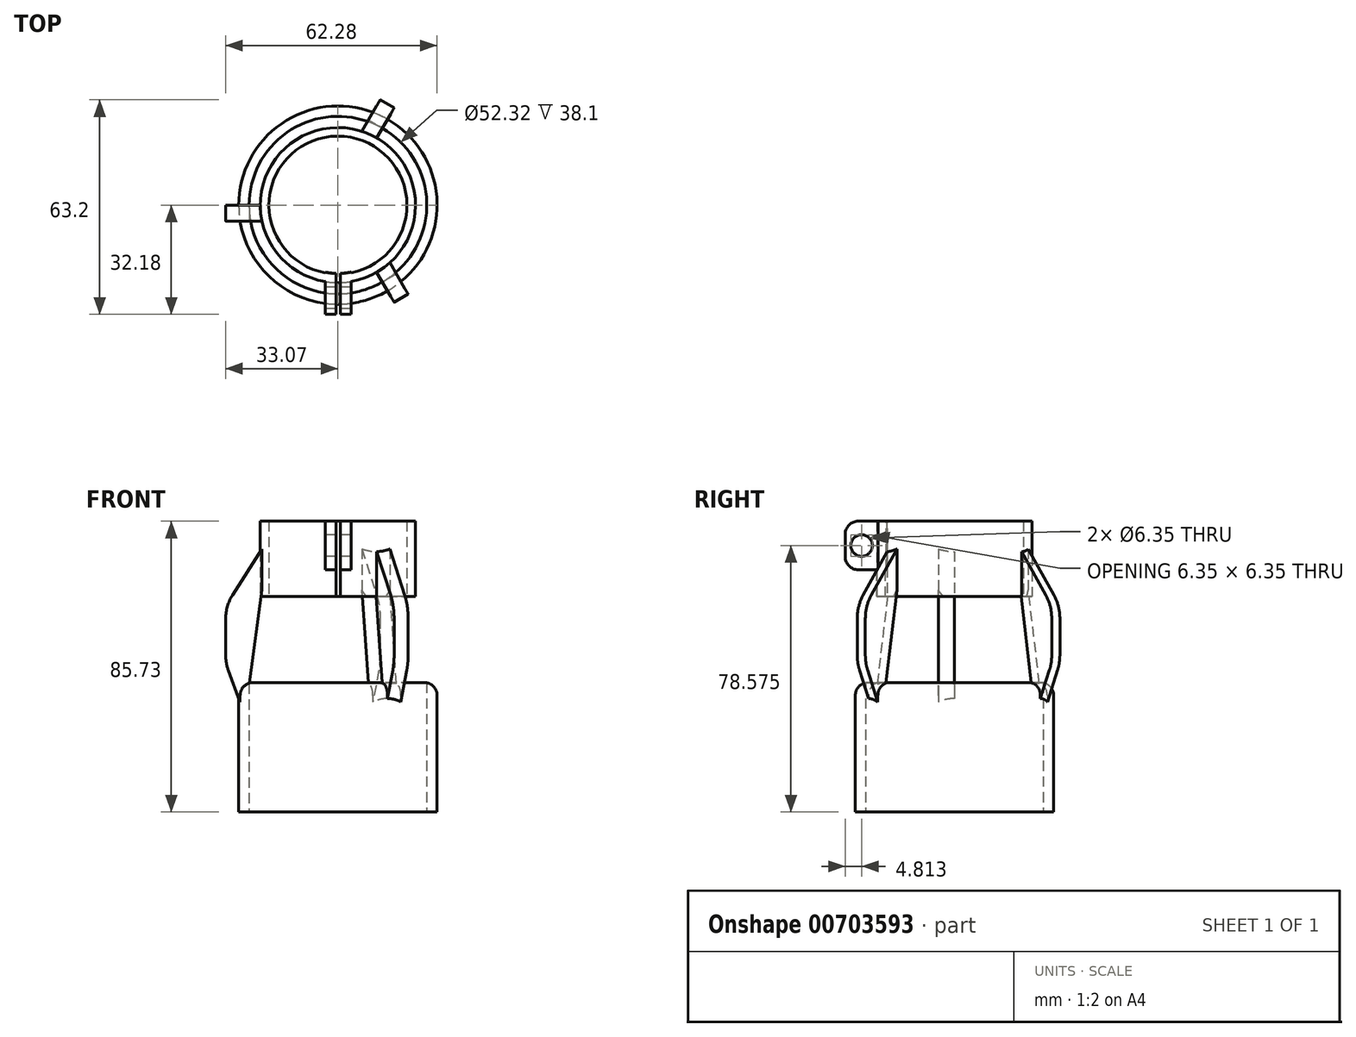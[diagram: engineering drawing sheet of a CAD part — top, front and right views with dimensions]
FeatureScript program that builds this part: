
annotation { "Feature Type Name" : "Feature", "Feature Type Description" : "" }
export const myFeature = defineFeature(function(context is Context, id is Id, definition is map)
    precondition{}
    {
        {
            var Q0;
            Q0=qCreatedBy(makeId("Top.planeOp"),FACE);
            var sketch = newSketch(context, id + "F0", { "sketchPlane" : qUnion([Q0])});
            skCircle(sketch, "E0", {"center": v(0, 0) * mm, "radius": 29.2 * mm});
            skCircle(sketch, "E1", {"center": v(0, 0) * mm, "radius": 26.16 * mm});
            skSolve(sketch);
        }
        {
            var Q0;
            Q0 = qSketchRegion(id + "F0", true);
            extrude(context, id + "F1", {"entities" : qUnion([Q0]), "depth" : 38.1 * mm, "offsetDistance" : 25.4 * mm});
        }
        {
            var Q0;
            Q0=makeQuery(id+"F1.opExtrude","CAP_FACE",FACE,{"disambiguationData":[OSD([sQuery(id+"F0.wireOp",EDGE,"E0"),sQuery(id+"F0.wireOp",EDGE,"E1")])],"isStart":false});
            cPlane(context, id + "F2", {"entities" : qUnion([Q0]), "cplaneType" : CPlaneType.OFFSET, "offset" : 25.4 * mm, "width" : 152.4 * mm, "height" : 152.4 * mm});
        }
        {
            var Q0;
            Q0=qCreatedBy(id+"F2.planeOp",FACE);
            var sketch = newSketch(context, id + "F3", { "sketchPlane" : qUnion([Q0])});
            skCircle(sketch, "E2", {"center": v(0, 0) * mm, "radius": 20.32 * mm});
            skCircle(sketch, "E3", {"center": v(0, 0) * mm, "radius": 22.86 * mm});
            skSolve(sketch);
        }
        {
            var Q0;
            Q0 = qSketchRegion(id + "F3", true);
            extrude(context, id + "F4", {"entities" : qUnion([Q0]), "depth" : 22.22 * mm, "offsetDistance" : 25.4 * mm});
        }
        {
            var Q0;
            Q0=makeQuery(id+"F4.opExtrude","CAP_FACE",FACE,{"disambiguationData":[OSD([sQuery(id+"F3.wireOp",EDGE,"E2"),sQuery(id+"F3.wireOp",EDGE,"E3")])],"isStart":false});
            var sketch = newSketch(context, id + "F5", { "sketchPlane" : qUnion([Q0])});
            skLineSegment(sketch, "E4", {"start": v(0, 0) * mm, "end": v(0, -32.55) * mm, "construction": true});
            skLineSegment(sketch, "E5", {"start": v(-0.54, 0.45) * mm, "end": v(0.73, 0.45) * mm});
            skLineSegment(sketch, "E6", {"start": v(0.73, 0.45) * mm, "end": v(0.73, -22.55) * mm});
            skLineSegment(sketch, "E7", {"start": v(-0.54, 0.45) * mm, "end": v(-0.54, -22.55) * mm});
            skLineSegment(sketch, "E8", {"start": v(0.73, 0.45) * mm, "end": v(3.9, 0.45) * mm});
            skLineSegment(sketch, "E9", {"start": v(3.9, 0.45) * mm, "end": v(-0.54, 0.45) * mm});
            skLineSegment(sketch, "E10", {"start": v(-0.54, 0.45) * mm, "end": v(-3.71, 0.45) * mm});
            skLineSegment(sketch, "E11", {"start": v(3.9, -22.52) * mm, "end": v(3.9, 0.45) * mm});
            skLineSegment(sketch, "E12", {"start": v(-3.71, 0.45) * mm, "end": v(-3.71, -32.18) * mm});
            skLineSegment(sketch, "E13", {"start": v(-3.71, -32.18) * mm, "end": v(-0.54, -32.18) * mm});
            skLineSegment(sketch, "E14", {"start": v(-0.54, -32.18) * mm, "end": v(-0.54, -22.55) * mm});
            skLineSegment(sketch, "E15", {"start": v(3.9, -22.52) * mm, "end": v(3.9, -32.18) * mm});
            skLineSegment(sketch, "E16", {"start": v(3.9, -32.18) * mm, "end": v(0.73, -32.18) * mm});
            skLineSegment(sketch, "E17", {"start": v(0.73, -32.18) * mm, "end": v(0.73, -22.55) * mm});
            skSolve(sketch);
        }
        {
            var Q0;
            Q0 = qSketchRegion(id + "F5", true);
            extrude(context, id + "F6", {"entities" : qUnion([Q0]), "operationType" : NewBodyOperationType.ADD, "oppositeDirection" : true, "depth" : 14.3 * mm, "offsetDistance" : 25.4 * mm});
        }
        {
            var Q0;
            Q0=makeQuery(id+"F6.boolean.opBoolean","MERGE",FACE,{"derivedFrom":[makeQuery(id+"F4.opExtrude","CAP_FACE",FACE,{"disambiguationData":[OSD([sQuery(id+"F3.wireOp",EDGE,"E2"),sQuery(id+"F3.wireOp",EDGE,"E3")])],"isStart":false}),makeQuery(id+"F6.opExtrude","CAP_FACE",FACE,{"disambiguationData":[OSD([sQuery(id+"F5.wireOp",EDGE,"E6"),sQuery(id+"F5.wireOp",EDGE,"E9"),sQuery(id+"F5.wireOp",EDGE,"E11"),sQuery(id+"F5.wireOp",EDGE,"E15"),sQuery(id+"F5.wireOp",EDGE,"E16"),sQuery(id+"F5.wireOp",EDGE,"E17")])],"isStart":true}),makeQuery(id+"F6.opExtrude","CAP_FACE",FACE,{"disambiguationData":[OSD([sQuery(id+"F5.wireOp",EDGE,"E7"),sQuery(id+"F5.wireOp",EDGE,"E10"),sQuery(id+"F5.wireOp",EDGE,"E12"),sQuery(id+"F5.wireOp",EDGE,"E13"),sQuery(id+"F5.wireOp",EDGE,"E14")])],"isStart":true})]});
            var sketch = newSketch(context, id + "F7", { "sketchPlane" : qUnion([Q0])});
            skCircle(sketch, "E18", {"center": v(0, 0) * mm, "radius": 20.13 * mm});
            skLineSegment(sketch, "E19", {"start": v(-0.54, -20.31) * mm, "end": v(-0.54, -22.85) * mm});
            skLineSegment(sketch, "E20", {"start": v(-0.54, -22.85) * mm, "end": v(0.73, -22.85) * mm});
            skLineSegment(sketch, "E21", {"start": v(0.73, -22.85) * mm, "end": v(0.73, -20.3) * mm});
            skLineSegment(sketch, "E22", {"start": v(0.73, -20.3) * mm, "end": v(-0.54, -20.31) * mm});
            skLineSegment(sketch, "E23", {"start": v(0.73, -20.3) * mm, "end": v(0.73, -19.94) * mm});
            skLineSegment(sketch, "E24", {"start": v(0.73, -19.94) * mm, "end": v(-0.54, -20.3) * mm});
            skLineSegment(sketch, "E25", {"start": v(-0.54, -20.3) * mm, "end": v(-0.54, -19.94) * mm});
            skLineSegment(sketch, "E26", {"start": v(-0.54, -19.94) * mm, "end": v(0.73, -19.94) * mm});
            skSolve(sketch);
        }
        {
            var Q0;
            {var subQ2=sQuery(id+"F5.wireOp",EDGE,"E12");var subQ5=sQuery(id+"F3.wireOp",EDGE,"E3");Q0=makeQuery(id+"F6.boolean.opBoolean","SPLIT",FACE,{"disambiguationData":[TD([makeQuery(id+"F4.opExtrude","SWEPT_FACE",FACE,{"disambiguationData":[OSD([subQ5])]})])],"derivedFrom":makeQuery(id+"F6.opExtrude","SWEPT_FACE",FACE,{"disambiguationData":[OSD([subQ2])]})});}
            var sketch = newSketch(context, id + "F8", { "sketchPlane" : qUnion([Q0])});
            skCircle(sketch, "E27", {"center": v(27.37, 78.57) * mm, "radius": 3.18 * mm});
            skPoint(sketch, "E27.centerSnap0", {"position": v(27.37, 85.72) * mm});
            skPoint(sketch, "E27.centerSnap1", {"position": v(22.56, 78.57) * mm});
            skSolve(sketch);
        }
        {
            var Q0;
            Q0=makeQuery(id+"F8.imprint","IMPRINT",FACE,{"disambiguationData":[TD([[makeQuery(id+"F8.imprint","IMPRINT",EDGE,{"derivedFrom":sQuery(id+"F8.wireOp",EDGE,"E27")}),1.0]])]});
            extrude(context, id + "F9", {"entities" : qUnion([Q0]), "operationType" : NewBodyOperationType.REMOVE, "oppositeDirection" : true, "depth" : 25.4 * mm, "offsetDistance" : 25.4 * mm});
        }
        {
            var Q0;
            Q0=makeQuery(id+"F6.opExtrude","CAP_EDGE",EDGE,{"disambiguationData":[OSD([sQuery(id+"F5.wireOp",EDGE,"E13")])],"isStart":true});
            var Q1;
            Q1=makeQuery(id+"F6.opExtrude","CAP_EDGE",EDGE,{"disambiguationData":[OSD([sQuery(id+"F5.wireOp",EDGE,"E16")])],"isStart":true});
            var Q2;
            Q2=makeQuery(id+"F6.opExtrude","CAP_EDGE",EDGE,{"disambiguationData":[OSD([sQuery(id+"F5.wireOp",EDGE,"E16")])],"isStart":false});
            var Q3;
            Q3=makeQuery(id+"F6.opExtrude","CAP_EDGE",EDGE,{"disambiguationData":[OSD([sQuery(id+"F5.wireOp",EDGE,"E13")])],"isStart":false});
            fillet(context, id + "F10", {"entities" : qUnion([Q0, Q1, Q2, Q3]), "radius" : 3.8 * mm, "tangentPropagation" : true, "allowEdgeOverflow" : false});
        }
        {
            var Q0;
            Q0 = qSketchRegion(id + "F7", true);
            extrude(context, id + "F11", {"entities" : qUnion([Q0]), "operationType" : NewBodyOperationType.REMOVE, "oppositeDirection" : true, "depth" : 25.4 * mm, "offsetDistance" : 25.4 * mm});
        }
        {
            var Q0;
            Q0=makeQuery(id+"F1.opExtrude","CAP_EDGE",EDGE,{"disambiguationData":[OSD([sQuery(id+"F0.wireOp",EDGE,"E0")])],"isStart":false});
            fillet(context, id + "F12", {"entities" : qUnion([Q0]), "radius" : 3.8 * mm, "tangentPropagation" : true, "allowEdgeOverflow" : false});
        }
        {
            var Q0;
            Q0=qCreatedBy(makeId("Front.planeOp"),FACE);
            var sketch = newSketch(context, id + "F13", { "sketchPlane" : qUnion([Q0])});
            skLineSegment(sketch, "E28", {"start": v(0, 0) * mm, "end": v(0, 124.18) * mm, "construction": true});
            skSolve(sketch);
        }
        {
            var Q0;
            Q0=qCreatedBy(makeId("Front.planeOp"),FACE);
            var sketch = newSketch(context, id + "F14", { "sketchPlane" : qUnion([Q0])});
            skLineSegment(sketch, "E29", {"start": v(-27.42, 28.63) * mm, "end": v(-21.24, 73.63) * mm});
            skLineSegment(sketch, "E30", {"start": v(-22.36, 77.57) * mm, "end": v(-33.07, 60.8) * mm});
            skPoint(sketch, "E30.startSnap0", {"position": v(-22.36, 75.6) * mm});
            skLineSegment(sketch, "E31", {"start": v(-33.07, 60.8) * mm, "end": v(-33.07, 43.97) * mm});
            skLineSegment(sketch, "E32", {"start": v(-33.07, 43.97) * mm, "end": v(-27.42, 28.63) * mm});
            skPoint(sketch, "E33.orphan", {"position": v(-23.49, 77.57) * mm});
            skLineSegment(sketch, "E34", {"start": v(-22.36, 77.57) * mm, "end": v(-21.24, 73.63) * mm});
            skSolve(sketch);
        }
        {
            var Q0;
            Q0 = qSketchRegion(id + "F14", true);
            extrude(context, id + "F15", {"entities" : qUnion([Q0]), "depth" : 4.76 * mm, "offsetDistance" : 25.4 * mm});
        }
        {
            var Q0;
            Q0=makeQuery(id+"F15.opExtrude","SWEPT_BODY",BODY,{"disambiguationData":[OSD([sQuery(id+"F14.wireOp",EDGE,"Suu7JAIw-Qndy-eXPM-zrnu-NCXWbo2hvGAh"),sQuery(id+"F14.wireOp",EDGE,"1IP7HeiN-rjTb-wPDy-BkEh-VjMk3GLwwtji"),sQuery(id+"F14.wireOp",EDGE,"PLsTwcUL-0GqW-qy0X-gp8w-Tw4aPqmEgGHP"),sQuery(id+"F14.wireOp",EDGE,"E29"),sQuery(id+"F14.wireOp",EDGE,"bjEwo6r7-lCPq-S24p-QCXI-rR8i7ekDdmNz")])]});
            var Q1;
            Q1=sQuery(id+"F13.wireOp",EDGE,"E28");
            circularPattern(context, id + "F16", {"operationType" : NewBodyOperationType.ADD, "entities" : qUnion([Q0]), "axis" : qUnion([Q1]), "angle" : 360 * degree, "instanceCount" : 3, "equalSpace" : true});
        }
        {
            var Q0;
            Q0=makeQuery(id+"F15.opExtrude","SWEPT_EDGE",EDGE,{"disambiguationData":[OSD([sQuery(id+"F14.wireOp",EDGE,"E30"),sQuery(id+"F14.wireOp",EDGE,"E31")])]});
            var Q1;
            Q1=makeQuery(id+"F15.opExtrude","SWEPT_EDGE",EDGE,{"disambiguationData":[OSD([sQuery(id+"F14.wireOp",EDGE,"E31"),sQuery(id+"F14.wireOp",EDGE,"E32")])]});
            fillet(context, id + "F17", {"entities" : qUnion([Q0, Q1]), "radius" : 12.7 * mm, "tangentPropagation" : true, "allowEdgeOverflow" : false});
        }
        {
            var Q0;
            Q0=makeQuery(id+"F16.opPattern","COPY",EDGE,{"derivedFrom":makeQuery(id+"F15.opExtrude","SWEPT_EDGE",EDGE,{"disambiguationData":[OSD([sQuery(id+"F14.wireOp",EDGE,"E30"),sQuery(id+"F14.wireOp",EDGE,"E31")])]}),"instanceName":"1"});
            var Q1;
            Q1=makeQuery(id+"F16.opPattern","COPY",EDGE,{"derivedFrom":makeQuery(id+"F15.opExtrude","SWEPT_EDGE",EDGE,{"disambiguationData":[OSD([sQuery(id+"F14.wireOp",EDGE,"E31"),sQuery(id+"F14.wireOp",EDGE,"E32")])]}),"instanceName":"1"});
            var Q2;
            Q2=makeQuery(id+"F16.opPattern","COPY",EDGE,{"derivedFrom":makeQuery(id+"F15.opExtrude","SWEPT_EDGE",EDGE,{"disambiguationData":[OSD([sQuery(id+"F14.wireOp",EDGE,"E30"),sQuery(id+"F14.wireOp",EDGE,"E31")])]}),"instanceName":"2"});
            var Q3;
            Q3=makeQuery(id+"F16.opPattern","COPY",EDGE,{"derivedFrom":makeQuery(id+"F15.opExtrude","SWEPT_EDGE",EDGE,{"disambiguationData":[OSD([sQuery(id+"F14.wireOp",EDGE,"E31"),sQuery(id+"F14.wireOp",EDGE,"E32")])]}),"instanceName":"2"});
            fillet(context, id + "F18", {"entities" : qUnion([Q0, Q1, Q2, Q3]), "radius" : 12.7 * mm, "tangentPropagation" : true, "allowEdgeOverflow" : false});
        }
    });
